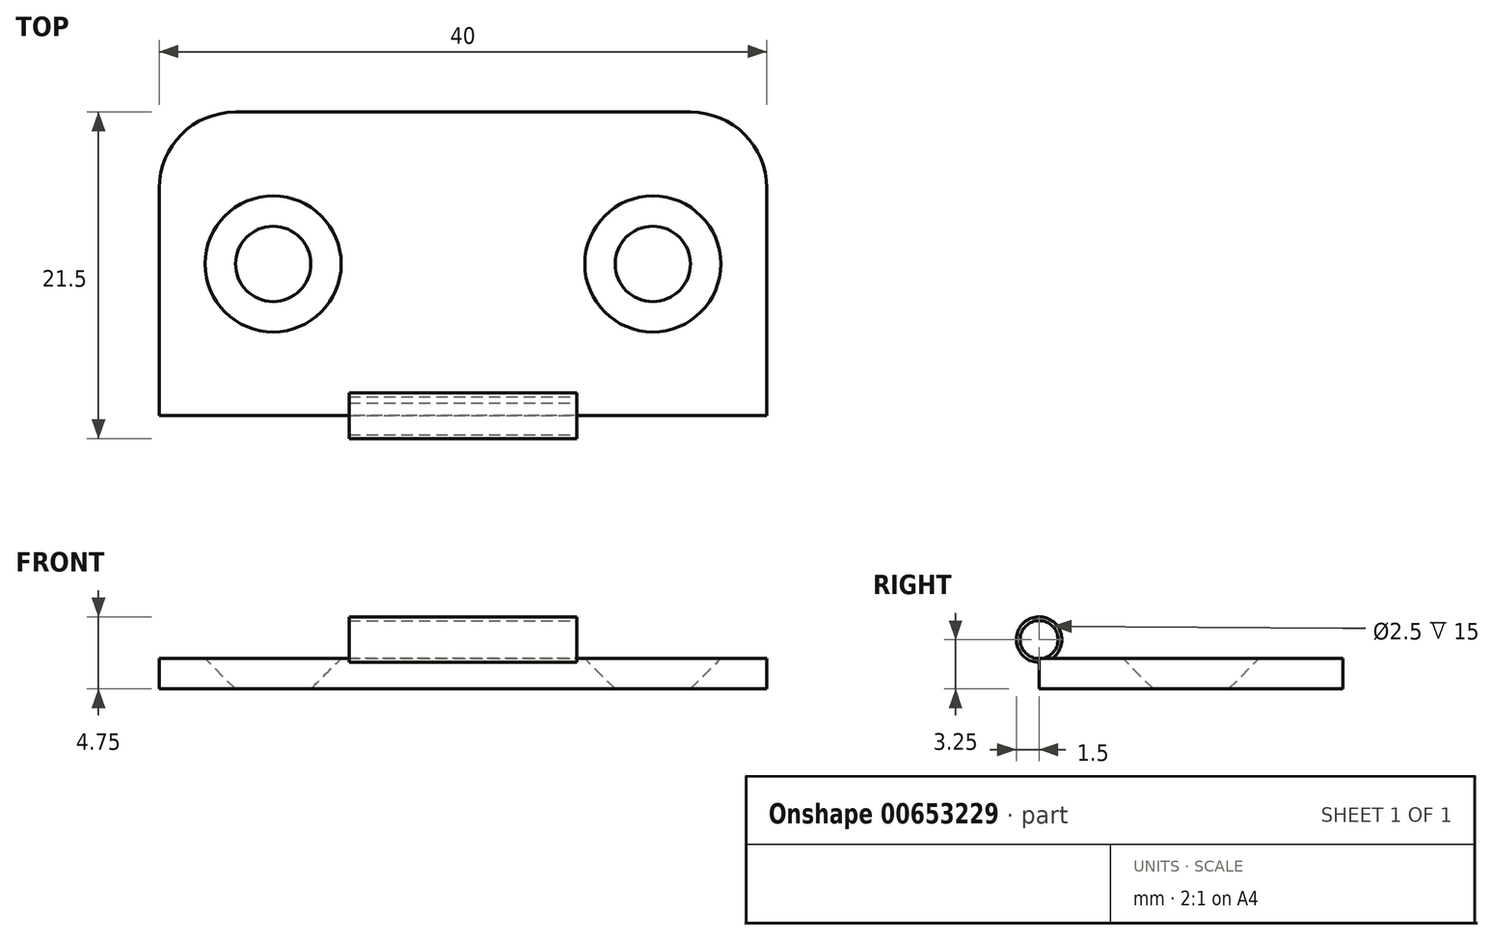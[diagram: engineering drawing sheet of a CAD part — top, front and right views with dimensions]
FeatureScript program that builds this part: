
annotation { "Feature Type Name" : "Feature", "Feature Type Description" : "" }
export const myFeature = defineFeature(function(context is Context, id is Id, definition is map)
    precondition{}
    {
        {
            var Q0;
            Q0=qCreatedBy(makeId("Top.planeOp"),FACE);
            var sketch = newSketch(context, id + "F0", { "sketchPlane" : qUnion([Q0])});
            skLineSegment(sketch, "E0.bottom", {"start": v(15, 10) * mm, "end": v(-15, 10) * mm});
            skLineSegment(sketch, "E0.top", {"start": v(20, -10) * mm, "end": v(-20, -10) * mm});
            skLineSegment(sketch, "E0.left", {"start": v(20, 5) * mm, "end": v(20, -10) * mm});
            skLineSegment(sketch, "E0.right", {"start": v(-20, 5) * mm, "end": v(-20, -10) * mm});
            skPoint(sketch, "E0.middle", {"position": v(0, 0) * mm});
            skPoint(sketch, "E1.visualSharp", {"position": v(-20, 10) * mm});
            skArc(sketch, "E1.filletArc", {"start": v(-15, 10) * mm, "mid": v(-18.54, 8.54) * mm, "end": v(-20, 5) * mm});
            skPoint(sketch, "E2.visualSharp", {"position": v(20, 10) * mm});
            skArc(sketch, "E2.filletArc", {"start": v(20, 5) * mm, "mid": v(18.54, 8.54) * mm, "end": v(15, 10) * mm});
            skSolve(sketch);
        }
        {
            var Q0;
            Q0=qSketchRegion(id+"F0",true);
            extrude(context, id + "F1", {"entities" : qUnion([Q0]), "depth" : 2 * mm, "offsetDistance" : 25 * mm});
        }
        {
            var Q0;
            Q0=makeQuery(id+"F1.opExtrude","SWEPT_FACE",FACE,{"disambiguationData":[OSD([sQuery(id+"F0.wireOp",EDGE,"E0.left")])]});
            cPlane(context, id + "F2", {"entities" : qUnion([Q0]), "cplaneType" : CPlaneType.OFFSET, "offset" : 12.5 * mm, "oppositeDirection" : true, "width" : 150 * mm, "height" : 150 * mm});
        }
        {
            var Q0;
            Q0=qCreatedBy(id+"F2.planeOp",FACE);
            var sketch = newSketch(context, id + "F3", { "sketchPlane" : qUnion([Q0])});
            skLineSegment(sketch, "E3.0", {"start": v(5, 2) * mm, "end": v(-10, 2) * mm, "construction": true});
            skLineSegment(sketch, "E4.0", {"start": v(-10, 2) * mm, "end": v(-10, 0) * mm, "construction": true});
            skCircle(sketch, "E5", {"center": v(-10, 3.25) * mm, "radius": 1.5 * mm});
            skSolve(sketch);
        }
        {
            var Q0;
            Q0=qCreatedBy(id+"F2.planeOp",FACE);
            cPlane(context, id + "F4", {"entities" : qUnion([Q0]), "cplaneType" : CPlaneType.OFFSET, "offset" : 15 * mm, "oppositeDirection" : true, "width" : 150 * mm, "height" : 150 * mm});
        }
        {
            var Q0;
            Q0=qSketchRegion(id+"F3",true);
            var Q1;
            Q1=qCreatedBy(id+"F4.planeOp",FACE);
            extrude(context, id + "F5", {"entities" : qUnion([Q0]), "operationType" : NewBodyOperationType.ADD, "endBound" : BoundingType.UP_TO_SURFACE, "oppositeDirection" : true, "depth" : 25 * mm, "endBoundEntityFace" : qUnion([Q1]), "offsetDistance" : 25 * mm});
        }
        {
            var Q0;
            {var subQ0=sQuery(id+"F0.wireOp",EDGE,"E0.left");Q0=makeQuery(id+"F5.boolean.opBoolean","MERGE",FACE,{"derivedFrom":[makeQuery(id+"F1.opExtrude","SWEPT_FACE",FACE,{"disambiguationData":[OSD([subQ0])]}),makeQuery(id+"F5.opExtrude","CAP_FACE",FACE,{"disambiguationData":[OSD([subQ0])],"isStart":false})]});}
            var sketch = newSketch(context, id + "F6", { "sketchPlane" : qUnion([Q0])});
            skArc(sketch, "E6.0", {"start": v(-9.17, 2) * mm, "mid": v(-10.43, 4.69) * mm, "end": v(-10, 1.75) * mm, "construction": true});
            skCircle(sketch, "E7", {"center": v(-10, 3.25) * mm, "radius": 1.25 * mm});
            skSolve(sketch);
        }
        {
            var Q0;
            Q0=qSketchRegion(id+"F6",true);
            var Q1;
            {var subQ0=sQuery(id+"F0.wireOp",EDGE,"E0.right");Q1=makeQuery(id+"FdmxAJekE3ElJXX_1.boolean.opBoolean","MERGE",FACE,{"derivedFrom":[makeQuery(id+"F1.opExtrude","SWEPT_FACE",FACE,{"disambiguationData":[OSD([subQ0])]}),makeQuery(id+"FdmxAJekE3ElJXX_1.opExtrude","CAP_FACE",FACE,{"disambiguationData":[OSD([subQ0])],"isStart":false})]});}
            extrude(context, id + "F7", {"entities" : qUnion([Q0]), "operationType" : NewBodyOperationType.REMOVE, "endBound" : BoundingType.UP_TO_SURFACE, "oppositeDirection" : true, "depth" : 25 * mm, "endBoundEntityFace" : qUnion([Q1]), "offsetDistance" : 25 * mm});
        }
        {
            var Q0;
            Q0=makeQuery(id+"F1.opExtrude","CAP_FACE",FACE,{"disambiguationData":[OSD([sQuery(id+"F0.wireOp",EDGE,"E0.bottom"),sQuery(id+"F0.wireOp",EDGE,"E0.top"),sQuery(id+"F0.wireOp",EDGE,"E0.left"),sQuery(id+"F0.wireOp",EDGE,"E0.right"),sQuery(id+"F0.wireOp",EDGE,"E1.filletArc"),sQuery(id+"F0.wireOp",EDGE,"E2.filletArc")])],"isStart":false});
            var sketch = newSketch(context, id + "F8", { "sketchPlane" : qUnion([Q0])});
            skPoint(sketch, "E8", {"position": v(-12.5, 0) * mm});
            skPoint(sketch, "E9", {"position": v(12.5, 0) * mm});
            skSolve(sketch);
        }
        {
            var Q0;
            Q0=sQuery(id+"F8.wireOp",VERTEX,"E8");
            var Q1;
            Q1=sQuery(id+"F8.wireOp",VERTEX,"E9");
            var Q2;
            Q2=makeQuery(id+"F1.opExtrude","SWEPT_BODY",BODY,{"disambiguationData":[OSD([sQuery(id+"F0.wireOp",EDGE,"E0.bottom"),sQuery(id+"F0.wireOp",EDGE,"E0.top"),sQuery(id+"F0.wireOp",EDGE,"E0.left"),sQuery(id+"F0.wireOp",EDGE,"E0.right"),sQuery(id+"F0.wireOp",EDGE,"E1.filletArc"),sQuery(id+"F0.wireOp",EDGE,"E2.filletArc")])]});
            hole(context, id + "F9", {"style" : HoleStyle.C_SINK, "endStyle" : HoleEndStyle.BLIND, "standardTappedOrClearance" : lookupTablePath({ "standard" : "ISO", "fit" : "Normal", "size" : "M4", "type" : "Clearance" }), "standardBlindInLast" : lookupTablePath({ "fit" : "Standard", "standard" : "ISO", "size" : "M4", "type" : "Clearance" }), "holeDiameter" : 4.4 * mm, "cSinkDiameter" : 8.96 * mm, "cSinkAngle" : 90 * degree, "majorDiameter" : 5 * mm, "holeDepth" : 14.1 * mm, "isTappedThrough" : true, "tappedDepth" : 12 * mm, "tapClearance" : 3, "startFromSketch" : true, "locations" : qUnion([Q0, Q1]), "scope" : qUnion([Q2])});
        }
    });
